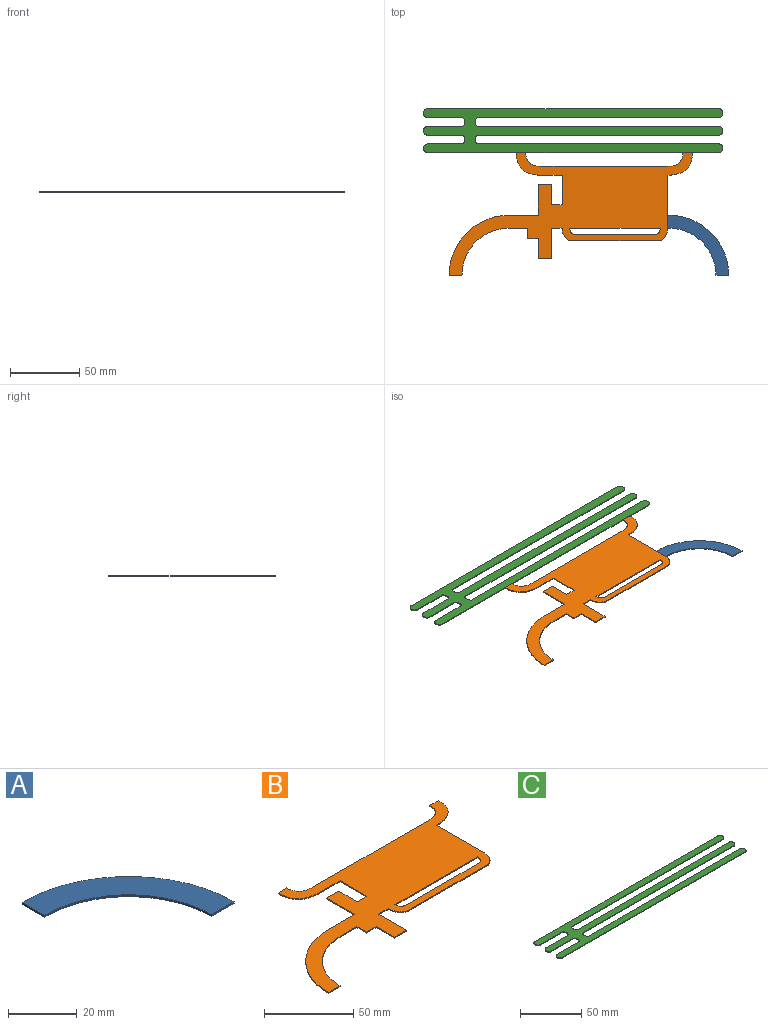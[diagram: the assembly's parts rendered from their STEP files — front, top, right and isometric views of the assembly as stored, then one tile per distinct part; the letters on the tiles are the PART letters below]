
ASSEMBLY  parts=3 mates=2
PART A: 7 faces, bbox 43.9x43.3x0.6 mm
  f0: cylinder r=34.04mm len=34.04mm, axis (0,0,-1), area 33.9mm2, adj f1,f4,f5,f6
  f1: plane 9.22x0.64mm, normal (0,-1,0), area 5.9mm2, adj f0,f2,f5,f6
  f2: cylinder r=43.26mm len=43.89mm, axis (0,0,-1), area 43.5mm2, adj f1,f3,f5,f6
  f3: plane 9.22x0.64mm, normal (-1,0,0), area 5.9mm2, adj f2,f4,f5,f6
  f4: plane 0.64x0.64mm, normal (0,-1,0), area 0.4mm2, adj f0,f3,f5,f6
  f5: plane 43.89x43.26mm, normal (0,0,1), area 565.6mm2, adj f0,f1,f2,f3,f4
  f6: plane 43.89x43.26mm, normal (0,0,-1), area 565.6mm2, adj f0,f1,f2,f3,f4
PART B: 34 faces, bbox 175.3x88.3x0.6 mm
  f0: extruded ~4.73x3.43mm, area 4mm2, adj f1,f31,f32,f33
  f1: plane 65.46x0.64mm, normal (0,-1,0), area 41.6mm2, adj f0,f2,f32,f33
  f2: extruded ~4.73x3.43mm, area 4mm2, adj f1,f31,f32,f33
  f3: extruded ~17.78x16.13mm, area 17.5mm2, adj f4,f30,f32,f33
  f4: plane 6.99x0.64mm, normal (0,1,0), area 4.4mm2, adj f3,f5,f32,f33
  f5: extruded ~10.8x9.78mm, area 10.7mm2, adj f4,f6,f32,f33
  f6: plane 91.44x0.64mm, normal (0,1,0), area 58.1mm2, adj f5,f7,f32,f33
  f7: extruded ~10.8x9.78mm, area 10.7mm2, adj f6,f8,f32,f33
  f8: plane 6.99x0.64mm, normal (0,1,0), area 4.4mm2, adj f7,f9,f32,f33
  f9: extruded ~17.78x16.13mm, area 17.5mm2, adj f8,f10,f32,f33
  f10: plane 15.24x0.64mm, normal (0,-1,0), area 9.7mm2, adj f9,f11,f32,f33
  f11: plane 21.26x0.64mm, normal (-1,0,0), area 13.5mm2, adj f10,f12,f32,f33
  f12: plane 7.62x0.64mm, normal (0,1,0), area 4.8mm2, adj f11,f13,f32,f33
  f13: plane 14.61x0.64mm, normal (1,0,0), area 9.3mm2, adj f12,f14,f32,f33
  f14: plane 9.53x0.64mm, normal (0,1,0), area 6mm2, adj f13,f15,f32,f33
  f15: plane 22.23x0.64mm, normal (-1,0,0), area 14.1mm2, adj f14,f16,f32,f33
  f16: plane 20.96x0.64mm, normal (0,1,0), area 13.3mm2, adj f15,f17,f32,f33
  f17: cylinder r=43.26mm len=43.26mm, axis (0,0,-1), area 43.1mm2, adj f16,f18,f32,f33
  f18: plane 9.22x0.64mm, normal (0,-1,0), area 5.9mm2, adj f17,f19,f32,f33
  f19: cylinder r=34.04mm len=34.04mm, axis (0,0,-1), area 33.9mm2, adj f18,f20,f32,f33
  f20: plane 13.34x0.64mm, normal (0,-1,0), area 8.5mm2, adj f19,f21,f32,f33
  f21: plane 7.62x0.64mm, normal (-1,0,0), area 4.8mm2, adj f20,f22,f32,f33
  f22: plane 7.62x0.64mm, normal (0,-1,0), area 4.8mm2, adj f21,f23,f32,f33
  f23: plane 14.61x0.64mm, normal (-1,0,0), area 9.3mm2, adj f22,f24,f32,f33
  f24: plane 9.53x0.64mm, normal (0,-1,0), area 6mm2, adj f23,f25,f32,f33
  f25: plane 22.23x0.64mm, normal (1,0,0), area 14.1mm2, adj f24,f26,f32,f33
  f26: plane 7.62x0.64mm, normal (0,-1,0), area 4.8mm2, adj f25,f27,f32,f33
  f27: extruded ~9.21x6.07mm, area 7.5mm2, adj f26,f28,f32,f33
  f28: plane 64.06x0.64mm, normal (0,-1,0), area 40.7mm2, adj f27,f29,f32,f33
  f29: extruded ~9.21x6.07mm, area 7.5mm2, adj f28,f30,f32,f33
  f30: plane 38.1x0.64mm, normal (1,0,0), area 24.2mm2, adj f3,f29,f32,f33
  f31: plane 58.59x0.64mm, normal (0,1,0), area 37.2mm2, adj f0,f2,f32,f33
  f32: plane 175.34x88.27mm, normal (0,0,1), area 5606.6mm2, adj f0,f1,f2,f3,f4,f5,f6,f7
  f33: plane 175.34x88.27mm, normal (0,0,-1), area 5606.6mm2, adj f0,f1,f2,f3,f4,f5,f6,f7
PART C: 22 faces, bbox 215.9x31.8x0.6 mm
  f0: plane 173.99x0.64mm, normal (0,1,0), area 110.5mm2, adj f1,f19,f20,f21
  f1: cylinder r=4.32mm len=6.35mm, axis (0,0,-1), area 4.5mm2, adj f0,f2,f20,f21
  f2: plane 173.99x0.64mm, normal (0,-1,0), area 110.5mm2, adj f1,f3,f20,f21
  f3: cylinder r=3.17mm len=6.35mm, axis (0,0,-1), area 6.3mm2, adj f2,f4,f20,f21
  f4: plane 209.55x0.64mm, normal (0,1,0), area 133.1mm2, adj f3,f5,f20,f21
  f5: cylinder r=3.17mm len=6.35mm, axis (0,0,-1), area 6.3mm2, adj f4,f6,f20,f21
  f6: plane 25.4x0.64mm, normal (0,-1,0), area 16.1mm2, adj f5,f7,f20,f21
  f7: cylinder r=4.32mm len=6.35mm, axis (0,0,-1), area 4.5mm2, adj f6,f8,f20,f21
  f8: plane 25.4x0.64mm, normal (0,1,0), area 16.1mm2, adj f7,f9,f20,f21
  f9: cylinder r=3.17mm len=6.35mm, axis (0,0,-1), area 6.3mm2, adj f8,f10,f20,f21
  f10: plane 25.4x0.64mm, normal (0,-1,0), area 16.1mm2, adj f9,f11,f20,f21
  f11: cylinder r=4.32mm len=6.35mm, axis (0,0,-1), area 4.5mm2, adj f10,f12,f20,f21
  f12: plane 25.4x0.64mm, normal (0,1,0), area 16.1mm2, adj f11,f13,f20,f21
  f13: cylinder r=3.17mm len=6.35mm, axis (0,0,-1), area 6.3mm2, adj f12,f14,f20,f21
  f14: plane 209.55x0.64mm, normal (0,-1,0), area 133.1mm2, adj f13,f15,f20,f21
  f15: cylinder r=3.17mm len=6.35mm, axis (0,0,-1), area 6.3mm2, adj f14,f16,f20,f21
  f16: plane 173.99x0.64mm, normal (0,1,0), area 110.5mm2, adj f15,f17,f20,f21
  f17: cylinder r=4.32mm len=6.35mm, axis (0,0,-1), area 4.5mm2, adj f16,f18,f20,f21
  f18: plane 173.99x0.64mm, normal (0,-1,0), area 110.5mm2, adj f17,f19,f20,f21
  f19: cylinder r=3.17mm len=6.35mm, axis (0,0,-1), area 6.3mm2, adj f0,f18,f20,f21
  f20: plane 215.9x31.75mm, normal (0,0,1), area 4191.5mm2, adj f0,f1,f2,f3,f4,f5,f6,f7
  f21: plane 215.9x31.75mm, normal (0,0,-1), area 4191.5mm2, adj f0,f1,f2,f3,f4,f5,f6,f7
PLACE A t=(9.8,-11.21,17.72)mm
PLACE B t=(9.8,-11.21,17.72)mm
PLACE C t=(-12.74,4.67,17.72)mm
MATE fastened A.f3 <-> B.f30  axis (-1,0,0) through (55.52,-65.44,18.03)mm
MATE fastened B.f4 <-> C.f14  axis (0,1,0) through (69.81,-11.21,18.03)mm
